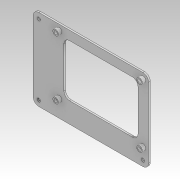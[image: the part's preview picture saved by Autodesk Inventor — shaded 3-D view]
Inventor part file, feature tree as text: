
AUTODESK INVENTOR PART (.ipt)
format: ipt  version: 2020 (Build 240168000, 168)  size: 149,504 bytes
history: native  units: mm
features: extrude x2, sketch x2
ambient origin geometry x8: Origin, YZ Plane, XZ Plane, XY Plane, X Axis, Y Axis, Z Axis, Center Point
bodies: Solid1 (feature_tree)
feature tree (4):
  extrude  "Extrusion1"  Depth=3.0mm
  extrude  "Extrusion2"  Depth=5.0mm
  sketch  "Sketch1"  dims[d0=74.1mm d1=52.0mm d2=3.0mm d3=45.0mm d4=6.0mm d5=0.0mm d8=62.0mm]
  sketch  "Sketch2"  dims[d9=92.0mm d10=5.0mm d11=5.0mm d12=5.0mm d13=5.0mm d14=5.0mm d15=5.0mm d16=3.0mm d17=1.5mm d18=0.0mm d19=5.0mm d20=3.0mm d21=0.0mm]
